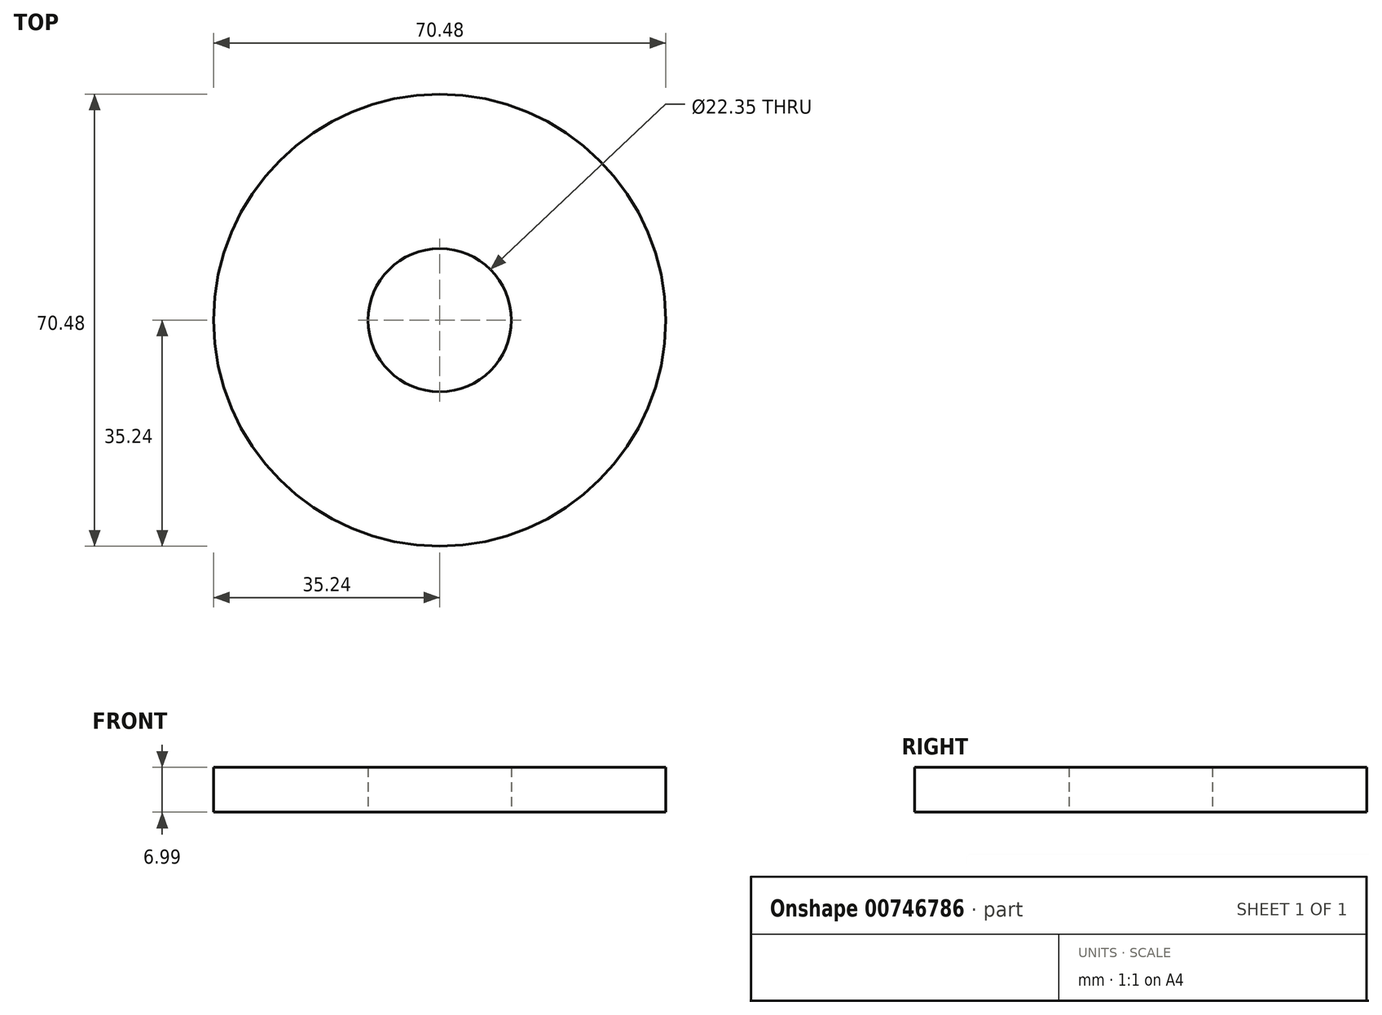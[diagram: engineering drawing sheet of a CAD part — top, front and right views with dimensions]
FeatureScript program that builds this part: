
annotation { "Feature Type Name" : "Feature", "Feature Type Description" : "" }
export const myFeature = defineFeature(function(context is Context, id is Id, definition is map)
    precondition{}
    {
        {
            var Q0;
            Q0=qCreatedBy(makeId("Top.planeOp"),FACE);
            var sketch = newSketch(context, id + "F0", { "sketchPlane" : qUnion([Q0])});
            skCircle(sketch, "E0", {"center": v(0, 0) * mm, "radius": 35.24 * mm});
            skCircle(sketch, "E1", {"center": v(0, 0) * mm, "radius": 11.18 * mm});
            skSolve(sketch);
        }
        {
            var Q0;
            Q0=makeQuery(id+"F0.imprint","IMPRINT",FACE,{"disambiguationData":[TD([[makeQuery(id+"F0.imprint","IMPRINT",EDGE,{"derivedFrom":sQuery(id+"F0.wireOp",EDGE,"E0")}),1.0]])]});
            var Q1;
            Q1=makeQuery(id+"F0.imprint","IMPRINT",FACE,{"disambiguationData":[TD([[makeQuery(id+"F0.imprint","IMPRINT",EDGE,{"derivedFrom":sQuery(id+"F0.wireOp",EDGE,"GsPD3Vca-tHw1-tpWf-YygS-qMUSOBv7om9t")}),1.0]])]});
            var Q2;
            Q2=makeQuery(id+"F0.imprint","IMPRINT",FACE,{"disambiguationData":[TD([[makeQuery(id+"F0.imprint","IMPRINT",EDGE,{"derivedFrom":sQuery(id+"F0.wireOp",EDGE,"E1")}),1.0]])]});
            var Q3;
            Q3=makeQuery(id+"F0.imprint","IMPRINT",FACE,{"disambiguationData":[TD([[makeQuery(id+"F0.imprint","IMPRINT",EDGE,{"derivedFrom":sQuery(id+"F0.wireOp",EDGE,"E1")}),-1.0]])]});
            extrude(context, id + "F1", {"entities" : qUnion([Q0, Q1, Q2, Q3]), "depth" : 7 * mm, "offsetDistance" : 25.4 * mm});
        }
        {
            var Q0;
            Q0=makeQuery(id+"F0.imprint","IMPRINT",FACE,{"disambiguationData":[TD([[makeQuery(id+"F0.imprint","IMPRINT",EDGE,{"derivedFrom":sQuery(id+"F0.wireOp",EDGE,"E1")}),1.0]])]});
            extrude(context, id + "F2", {"entities" : qUnion([Q0]), "operationType" : NewBodyOperationType.REMOVE, "endBound" : BoundingType.THROUGH_ALL, "depth" : 25.4 * mm, "offsetDistance" : 25.4 * mm});
        }
    });
